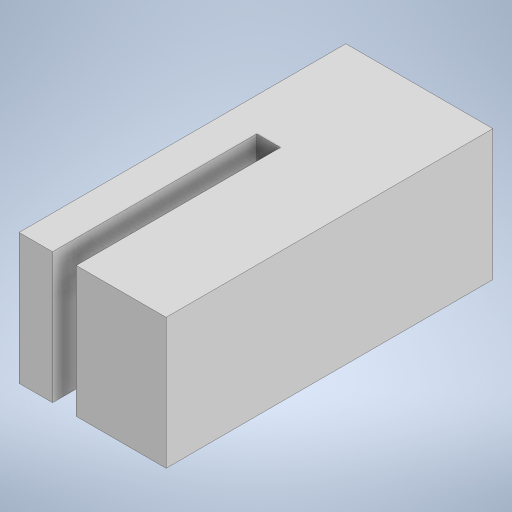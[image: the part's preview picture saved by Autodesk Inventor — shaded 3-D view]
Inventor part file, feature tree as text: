
AUTODESK INVENTOR PART (.ipt)
format: ipt  version: 2023 (Build 270158000, 158)  size: 190,464 bytes
history: native  units: in
note: dims shown in document units (in); Inventor stores cm internally (conversion verified against a paired STEP export)
features: extrude x2, sketch x2
ambient origin geometry x8: Origin, YZ Plane, XZ Plane, XY Plane, X Axis, Y Axis, Z Axis, Center Point
bodies: Solid1 (feature_tree)
feature tree (4):
  extrude  "Extrusion1"  Depth=1.0in
  extrude  "Extrusion2"  Depth=0.275in
  sketch  "Sketch1"  dims[d0=0.45in d1=1.0in]
  sketch  "Sketch2"  dims[d2=0.4in d3=0.0in d4=0.275in d5=0.0725in d6=0.625in d7=0.5in d8=0.0in]
